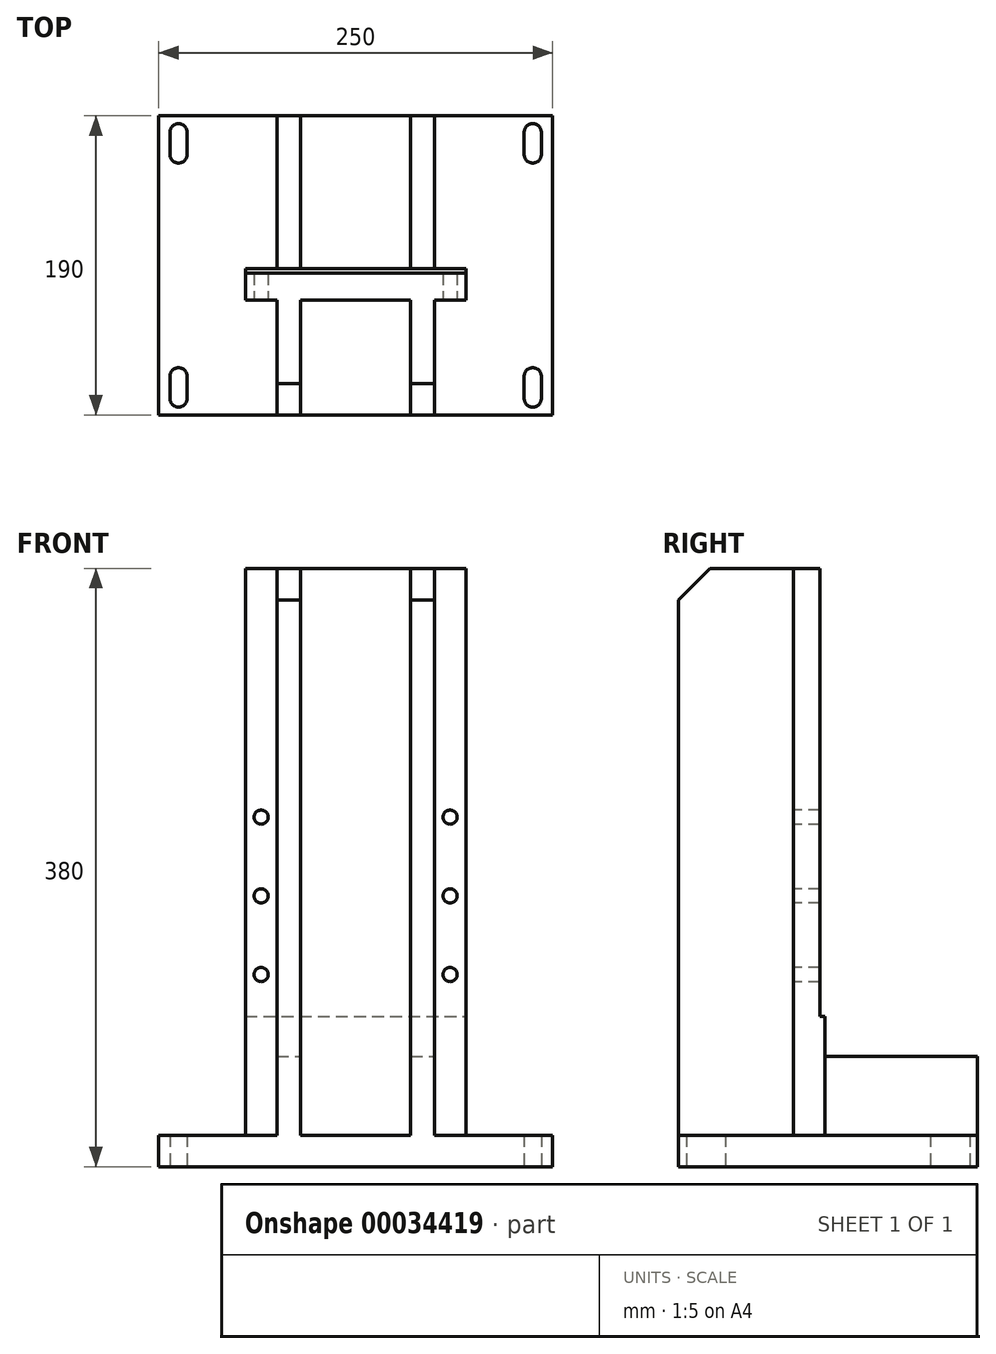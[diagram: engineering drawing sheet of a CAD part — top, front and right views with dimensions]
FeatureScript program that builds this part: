
annotation { "Feature Type Name" : "Feature", "Feature Type Description" : "" }
export const myFeature = defineFeature(function(context is Context, id is Id, definition is map)
    precondition{}
    {
        {
            var Q0;
            Q0=qCreatedBy(makeId("Top.planeOp"),FACE);
            var sketch = newSketch(context, id + "F0", { "sketchPlane" : qUnion([Q0])});
            skLineSegment(sketch, "E0.bottom", {"start": v(125, -95) * mm, "end": v(-125, -95) * mm});
            skLineSegment(sketch, "E0.top", {"start": v(125, 95) * mm, "end": v(-125, 95) * mm});
            skLineSegment(sketch, "E0.left", {"start": v(125, -95) * mm, "end": v(125, 95) * mm});
            skLineSegment(sketch, "E0.right", {"start": v(-125, -95) * mm, "end": v(-125, 95) * mm});
            skPoint(sketch, "E0.middle", {"position": v(0, 0) * mm});
            skLineSegment(sketch, "E1", {"start": v(-112.5, 94.44) * mm, "end": v(-112.5, 60.56) * mm, "construction": true});
            skLineSegment(sketch, "E2.bottom", {"start": v(-107, 84.5) * mm, "end": v(-118, 84.5) * mm, "construction": true});
            skLineSegment(sketch, "E2.top", {"start": v(-107, 70.5) * mm, "end": v(-118, 70.5) * mm, "construction": true});
            skLineSegment(sketch, "E2.left", {"start": v(-107, 84.5) * mm, "end": v(-107, 70.5) * mm});
            skLineSegment(sketch, "E2.right", {"start": v(-118, 84.5) * mm, "end": v(-118, 70.5) * mm});
            skPoint(sketch, "E2.middle", {"position": v(-112.5, 77.5) * mm});
            skArc(sketch, "E3", {"start": v(-118, 84.5) * mm, "mid": v(-112.5, 90) * mm, "end": v(-107, 84.5) * mm});
            skArc(sketch, "E4", {"start": v(-118, 70.5) * mm, "mid": v(-112.5, 65) * mm, "end": v(-107, 70.5) * mm});
            skArc(sketch, "E5.0.1.0", {"start": v(-118, -84.5) * mm, "mid": v(-112.5, -90) * mm, "end": v(-107, -84.5) * mm});
            skPoint(sketch, "E5.0.1.1", {"position": v(-112.5, -77.5) * mm});
            skLineSegment(sketch, "E5.0.1.2", {"start": v(-107, -70.5) * mm, "end": v(-107, -84.5) * mm});
            skLineSegment(sketch, "E5.0.1.3", {"start": v(-107, -84.5) * mm, "end": v(-118, -84.5) * mm, "construction": true});
            skLineSegment(sketch, "E5.0.1.4", {"start": v(-112.5, -60.56) * mm, "end": v(-112.5, -94.44) * mm, "construction": true});
            skLineSegment(sketch, "E5.0.1.5", {"start": v(-107, -70.5) * mm, "end": v(-118, -70.5) * mm, "construction": true});
            skArc(sketch, "E5.0.1.6", {"start": v(-118, -70.5) * mm, "mid": v(-112.5, -65) * mm, "end": v(-107, -70.5) * mm});
            skLineSegment(sketch, "E5.0.1.7", {"start": v(-118, -70.5) * mm, "end": v(-118, -84.5) * mm});
            skArc(sketch, "E5.1.0.0", {"start": v(107, 70.5) * mm, "mid": v(112.5, 65) * mm, "end": v(118, 70.5) * mm});
            skPoint(sketch, "E5.1.0.1", {"position": v(112.5, 77.5) * mm});
            skLineSegment(sketch, "E5.1.0.2", {"start": v(118, 84.5) * mm, "end": v(118, 70.5) * mm});
            skLineSegment(sketch, "E5.1.0.3", {"start": v(118, 70.5) * mm, "end": v(107, 70.5) * mm, "construction": true});
            skLineSegment(sketch, "E5.1.0.4", {"start": v(112.5, 94.44) * mm, "end": v(112.5, 60.56) * mm, "construction": true});
            skLineSegment(sketch, "E5.1.0.5", {"start": v(118, 84.5) * mm, "end": v(107, 84.5) * mm, "construction": true});
            skArc(sketch, "E5.1.0.6", {"start": v(107, 84.5) * mm, "mid": v(112.5, 90) * mm, "end": v(118, 84.5) * mm});
            skLineSegment(sketch, "E5.1.0.7", {"start": v(107, 84.5) * mm, "end": v(107, 70.5) * mm});
            skArc(sketch, "E5.1.1.0", {"start": v(107, -84.5) * mm, "mid": v(112.5, -90) * mm, "end": v(118, -84.5) * mm});
            skPoint(sketch, "E5.1.1.1", {"position": v(112.5, -77.5) * mm});
            skLineSegment(sketch, "E5.1.1.2", {"start": v(118, -70.5) * mm, "end": v(118, -84.5) * mm});
            skLineSegment(sketch, "E5.1.1.3", {"start": v(118, -84.5) * mm, "end": v(107, -84.5) * mm, "construction": true});
            skLineSegment(sketch, "E5.1.1.4", {"start": v(112.5, -60.56) * mm, "end": v(112.5, -94.44) * mm, "construction": true});
            skLineSegment(sketch, "E5.1.1.5", {"start": v(118, -70.5) * mm, "end": v(107, -70.5) * mm, "construction": true});
            skArc(sketch, "E5.1.1.6", {"start": v(107, -70.5) * mm, "mid": v(112.5, -65) * mm, "end": v(118, -70.5) * mm});
            skLineSegment(sketch, "E5.1.1.7", {"start": v(107, -70.5) * mm, "end": v(107, -84.5) * mm});
            skLineSegment(sketch, "E5.direction1", {"start": v(-112.5, 77.5) * mm, "end": v(112.5, 77.5) * mm, "construction": true});
            skLineSegment(sketch, "E5.direction2", {"start": v(-112.5, 77.5) * mm, "end": v(-112.5, -77.5) * mm, "construction": true});
            skSolve(sketch);
        }
        {
            var Q0;
            Q0 = qSketchRegion(id + "F0", true);
            extrude(context, id + "F1", {"entities" : qUnion([Q0]), "depth" : 20 * mm});
        }
        {
            var Q0;
            Q0=makeQuery(id+"F1.opExtrude","CAP_FACE",FACE,{"disambiguationData":[OSD([sQuery(id+"F0.wireOp",EDGE,"E0.bottom"),sQuery(id+"F0.wireOp",EDGE,"E0.top"),sQuery(id+"F0.wireOp",EDGE,"E0.left"),sQuery(id+"F0.wireOp",EDGE,"E0.right"),sQuery(id+"F0.wireOp",EDGE,"E2.left"),sQuery(id+"F0.wireOp",EDGE,"E2.right"),sQuery(id+"F0.wireOp",EDGE,"E3"),sQuery(id+"F0.wireOp",EDGE,"E4"),sQuery(id+"F0.wireOp",EDGE,"E5.0.1.0"),sQuery(id+"F0.wireOp",EDGE,"E5.0.1.2"),sQuery(id+"F0.wireOp",EDGE,"E5.0.1.6"),sQuery(id+"F0.wireOp",EDGE,"E5.0.1.7"),sQuery(id+"F0.wireOp",EDGE,"E5.1.0.0"),sQuery(id+"F0.wireOp",EDGE,"E5.1.0.2"),sQuery(id+"F0.wireOp",EDGE,"E5.1.0.6"),sQuery(id+"F0.wireOp",EDGE,"E5.1.0.7"),sQuery(id+"F0.wireOp",EDGE,"E5.1.1.0"),sQuery(id+"F0.wireOp",EDGE,"E5.1.1.2"),sQuery(id+"F0.wireOp",EDGE,"E5.1.1.6"),sQuery(id+"F0.wireOp",EDGE,"E5.1.1.7")])],"isStart":false});
            var sketch = newSketch(context, id + "F2", { "sketchPlane" : qUnion([Q0])});
            skLineSegment(sketch, "E6.0", {"start": v(-125, -95) * mm, "end": v(-125, 95) * mm});
            skLineSegment(sketch, "E7", {"start": v(-35, -22) * mm, "end": v(-35, -95) * mm});
            skLineSegment(sketch, "E8", {"start": v(-50, -95) * mm, "end": v(-35, -95) * mm});
            skLineSegment(sketch, "E9", {"start": v(-50, -95) * mm, "end": v(-50, -22) * mm});
            skLineSegment(sketch, "E10", {"start": v(35, -22) * mm, "end": v(35, -95) * mm});
            skLineSegment(sketch, "E11", {"start": v(35, -95) * mm, "end": v(50, -95) * mm});
            skLineSegment(sketch, "E12", {"start": v(50, -95) * mm, "end": v(50, -22) * mm});
            skLineSegment(sketch, "E13", {"start": v(50, -22) * mm, "end": v(35, -22) * mm});
            skLineSegment(sketch, "E14", {"start": v(-50, -22) * mm, "end": v(-35, -22) * mm});
            skLineSegment(sketch, "E15.bottom", {"start": v(70, -22) * mm, "end": v(-70, -22) * mm});
            skLineSegment(sketch, "E15.top", {"start": v(70, -2) * mm, "end": v(-70, -2) * mm});
            skLineSegment(sketch, "E15.left", {"start": v(70, -22) * mm, "end": v(70, -2) * mm});
            skLineSegment(sketch, "E15.right", {"start": v(-70, -22) * mm, "end": v(-70, -2) * mm});
            skPoint(sketch, "E15.middle", {"position": v(0, 0) * mm});
            skLineSegment(sketch, "E16", {"start": v(-50, -2) * mm, "end": v(-50, 95) * mm});
            skLineSegment(sketch, "E17", {"start": v(-50, 95) * mm, "end": v(-35, 95) * mm});
            skLineSegment(sketch, "E18", {"start": v(-35, 95) * mm, "end": v(-35, -2) * mm});
            skLineSegment(sketch, "E19", {"start": v(35, -2) * mm, "end": v(35, 95) * mm});
            skLineSegment(sketch, "E20", {"start": v(35, 95) * mm, "end": v(50, 95) * mm});
            skLineSegment(sketch, "E21", {"start": v(50, 95) * mm, "end": v(50, -2) * mm});
            skLineSegment(sketch, "E22", {"start": v(50, -2) * mm, "end": v(35, -2) * mm});
            skSolve(sketch);
        }
        {
            var Q0;
            {var subQ0=sQuery(id+"F2.wireOp",EDGE,"E7");Q0=makeQuery(id+"F2.imprint","IMPRINT",FACE,{"disambiguationData":[TD([[makeQuery(id+"F2.imprint","IMPRINT",EDGE,{"derivedFrom":subQ0}),-1.0]])]});}
            var Q1;
            {var subQ0=sQuery(id+"F2.wireOp",EDGE,"E10");Q1=makeQuery(id+"F2.imprint","IMPRINT",FACE,{"disambiguationData":[TD([[makeQuery(id+"F2.imprint","IMPRINT",EDGE,{"derivedFrom":subQ0}),1.0]])]});}
            var Q2;
            {var subQ8=sQuery(id+"F2.wireOp",EDGE,"E15.left");Q2=makeQuery(id+"F2.imprint","IMPRINT",FACE,{"disambiguationData":[TD([[makeQuery(id+"F2.imprint","IMPRINT",EDGE,{"derivedFrom":subQ8}),1.0]])]});}
            var Q3;
            Q3=makeQuery(id+"F2.imprint","IMPRINT",FACE,{"disambiguationData":[TD([[makeQuery(id+"F2.imprint","IMPRINT",EDGE,{"derivedFrom":sQuery(id+"F2.wireOp",EDGE,"E19")}),-1.0]])]});
            var Q4;
            {var subQ0=sQuery(id+"F2.wireOp",EDGE,"E16");Q4=makeQuery(id+"F2.imprint","IMPRINT",FACE,{"disambiguationData":[TD([[makeQuery(id+"F2.imprint","IMPRINT",EDGE,{"derivedFrom":subQ0}),-1.0]])]});}
            extrude(context, id + "F3", {"entities" : qUnion([Q0, Q1, Q2, Q3, Q4]), "operationType" : NewBodyOperationType.ADD, "depth" : 360 * mm});
        }
        {
            var Q0;
            Q0=makeQuery(id+"F3.opExtrude","SWEPT_FACE",FACE,{"disambiguationData":[OSD([sQuery(id+"F2.wireOp",EDGE,"E21")])]});
            var sketch = newSketch(context, id + "F4", { "sketchPlane" : qUnion([Q0])});
            skLineSegment(sketch, "E23.0", {"start": v(-95, 20) * mm, "end": v(95, 20) * mm, "construction": true});
            skLineSegment(sketch, "E24", {"start": v(95, 70) * mm, "end": v(-2, 70) * mm});
            skLineSegment(sketch, "E25", {"start": v(-2, 70) * mm, "end": v(-2, 380) * mm});
            skLineSegment(sketch, "E26", {"start": v(-2, 380) * mm, "end": v(95, 380) * mm});
            skLineSegment(sketch, "E27", {"start": v(95, 380) * mm, "end": v(95, 70) * mm});
            skLineSegment(sketch, "E28", {"start": v(-2, 380) * mm, "end": v(-2, 95.44) * mm});
            skLineSegment(sketch, "E29", {"start": v(-2, 95.44) * mm, "end": v(-5, 95.44) * mm});
            skLineSegment(sketch, "E30", {"start": v(-5, 95.44) * mm, "end": v(-5, 380) * mm});
            skLineSegment(sketch, "E31", {"start": v(-5, 380) * mm, "end": v(-2, 380) * mm});
            skSolve(sketch);
        }
        {
            var Q0;
            Q0 = qSketchRegion(id + "F4", true);
            extrude(context, id + "F5", {"entities" : qUnion([Q0]), "operationType" : NewBodyOperationType.REMOVE, "oppositeDirection" : true, "depth" : 280 * mm, "symmetric" : true});
        }
        {
            var Q0;
            Q0=makeQuery(id+"F3.opExtrude","CAP_EDGE",EDGE,{"disambiguationData":[OSD([sQuery(id+"F2.wireOp",EDGE,"E11")])],"isStart":false});
            var Q1;
            Q1=makeQuery(id+"F3.opExtrude","CAP_EDGE",EDGE,{"disambiguationData":[OSD([sQuery(id+"F2.wireOp",EDGE,"E8")])],"isStart":false});
            var Q2;
            {var subQ0=sQuery(id+"F2.wireOp",EDGE,"E20");var subQ1=sQuery(id+"F0.wireOp",EDGE,"E0.top");var subQ2=sQuery(id+"F2.wireOp",EDGE,"E21");var subQ3=sQuery(id+"F4.wireOp",EDGE,"E24");Q2=makeQuery(id+"F5.boolean.opBoolean","COPY",EDGE,{"disambiguationData":[TD([makeQuery(id+"F3.opExtrude","SWEPT_FACE",FACE,{"disambiguationData":[OSD([sQuery(id+"F2.wireOp",EDGE,"E19")])]})])],"derivedFrom":makeQuery(id+"F5.opExtrude","SWEPT_EDGE",EDGE,{"disambiguationData":[OSD([subQ1,subQ0,subQ2,subQ3,sQuery(id+"F4.wireOp",EDGE,"E27")])]})});}
            var Q3;
            {var subQ0=sQuery(id+"F0.wireOp",EDGE,"E0.top");var subQ1=sQuery(id+"F2.wireOp",EDGE,"E20");var subQ2=sQuery(id+"F4.wireOp",EDGE,"E24");Q3=makeQuery(id+"F5.boolean.opBoolean","COPY",EDGE,{"disambiguationData":[TD([makeQuery(id+"F3.opExtrude","SWEPT_FACE",FACE,{"disambiguationData":[OSD([sQuery(id+"F2.wireOp",EDGE,"E16")])]})])],"derivedFrom":makeQuery(id+"F5.opExtrude","SWEPT_EDGE",EDGE,{"disambiguationData":[OSD([subQ0,subQ1,sQuery(id+"F2.wireOp",EDGE,"E21"),subQ2,sQuery(id+"F4.wireOp",EDGE,"E27")])]})});}
            chamfer(context, id + "F6", {"entities" : qUnion([Q0, Q1, Q2, Q3]), "width" : (20) * mm, "tangentPropagation" : true});
        }
        {
            var Q0;
            {var subQ0=sQuery(id+"F2.wireOp",EDGE,"E15.bottom");Q0=makeQuery(id+"F3.opExtrude","SWEPT_FACE",FACE,{"disambiguationData":[OSD([subQ0]),TDD([makeQuery(id+"F2.imprint","IMPRINT",EDGE,{"disambiguationData":[TD([[makeQuery(id+"F2.imprint","INTERSECT",VERTEX,{"derivedFrom":[sQuery(id+"F2.wireOp",EDGE,"E9"),subQ0]}),-1.0]])],"derivedFrom":subQ0})])]});}
            var sketch = newSketch(context, id + "F7", { "sketchPlane" : qUnion([Q0])});
            skPoint(sketch, "E32", {"position": v(-60, 222) * mm});
            skPoint(sketch, "E33", {"position": v(-60, 172) * mm});
            skPoint(sketch, "E34", {"position": v(-60, 122) * mm});
            skPoint(sketch, "E35", {"position": v(60, 222) * mm});
            skPoint(sketch, "E36", {"position": v(60, 172) * mm});
            skPoint(sketch, "E37", {"position": v(60, 122) * mm});
            skSolve(sketch);
        }
        {
            var Q0;
            Q0=sQuery(id+"F7.wireOp",VERTEX,"E32");
            var Q1;
            Q1=sQuery(id+"F7.wireOp",VERTEX,"E33");
            var Q2;
            Q2=sQuery(id+"F7.wireOp",VERTEX,"E34");
            var Q3;
            Q3=sQuery(id+"F7.wireOp",VERTEX,"E35");
            var Q4;
            Q4=sQuery(id+"F7.wireOp",VERTEX,"E36");
            var Q5;
            Q5=sQuery(id+"F7.wireOp",VERTEX,"E37");
            var Q6;
            Q6=makeQuery(id+"F1.opExtrude","SWEPT_BODY",BODY,{"disambiguationData":[OSD([sQuery(id+"F0.wireOp",EDGE,"E0.bottom"),sQuery(id+"F0.wireOp",EDGE,"E0.top"),sQuery(id+"F0.wireOp",EDGE,"E0.left"),sQuery(id+"F0.wireOp",EDGE,"E0.right"),sQuery(id+"F0.wireOp",EDGE,"E2.left"),sQuery(id+"F0.wireOp",EDGE,"E2.right"),sQuery(id+"F0.wireOp",EDGE,"E3"),sQuery(id+"F0.wireOp",EDGE,"E4"),sQuery(id+"F0.wireOp",EDGE,"E5.0.1.0"),sQuery(id+"F0.wireOp",EDGE,"E5.0.1.2"),sQuery(id+"F0.wireOp",EDGE,"E5.0.1.6"),sQuery(id+"F0.wireOp",EDGE,"E5.0.1.7"),sQuery(id+"F0.wireOp",EDGE,"E5.1.0.0"),sQuery(id+"F0.wireOp",EDGE,"E5.1.0.2"),sQuery(id+"F0.wireOp",EDGE,"E5.1.0.6"),sQuery(id+"F0.wireOp",EDGE,"E5.1.0.7"),sQuery(id+"F0.wireOp",EDGE,"E5.1.1.0"),sQuery(id+"F0.wireOp",EDGE,"E5.1.1.2"),sQuery(id+"F0.wireOp",EDGE,"E5.1.1.6"),sQuery(id+"F0.wireOp",EDGE,"E5.1.1.7")])]});
            hole(context, id + "F8", {"style" : HoleStyle.SIMPLE, "endStyle" : HoleEndStyle.THROUGH, "holeDiameter" : 9 * mm, "tappedDepth" : 12 * mm, "tapClearance" : 3, "locations" : qUnion([Q0, Q1, Q2, Q3, Q4, Q5]), "scope" : qUnion([Q6])});
        }
    });
